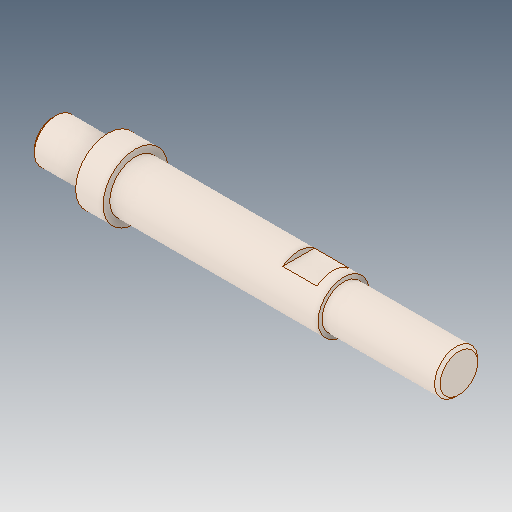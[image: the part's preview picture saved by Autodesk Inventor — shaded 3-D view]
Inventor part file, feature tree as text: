
AUTODESK INVENTOR PART (.ipt)
format: ipt  version: 2019 (Build 230136000, 136)  size: 116,224 bytes
history: native  units: mm
features: chamfer x1
ambient origin geometry x8: Origin, YZ Plane, XZ Plane, XY Plane, X Axis, Y Axis, Z Axis, Center Point
bodies: Solid1 (feature_tree)
feature tree (1):
  chamfer  "Chamfer3"  [1 undecoded]
note: 1 required parameter value undecoded (feature->parameter linkage not recoverable at this tier; creation-order binding heuristic only, values carry confidence <= 0.55)
